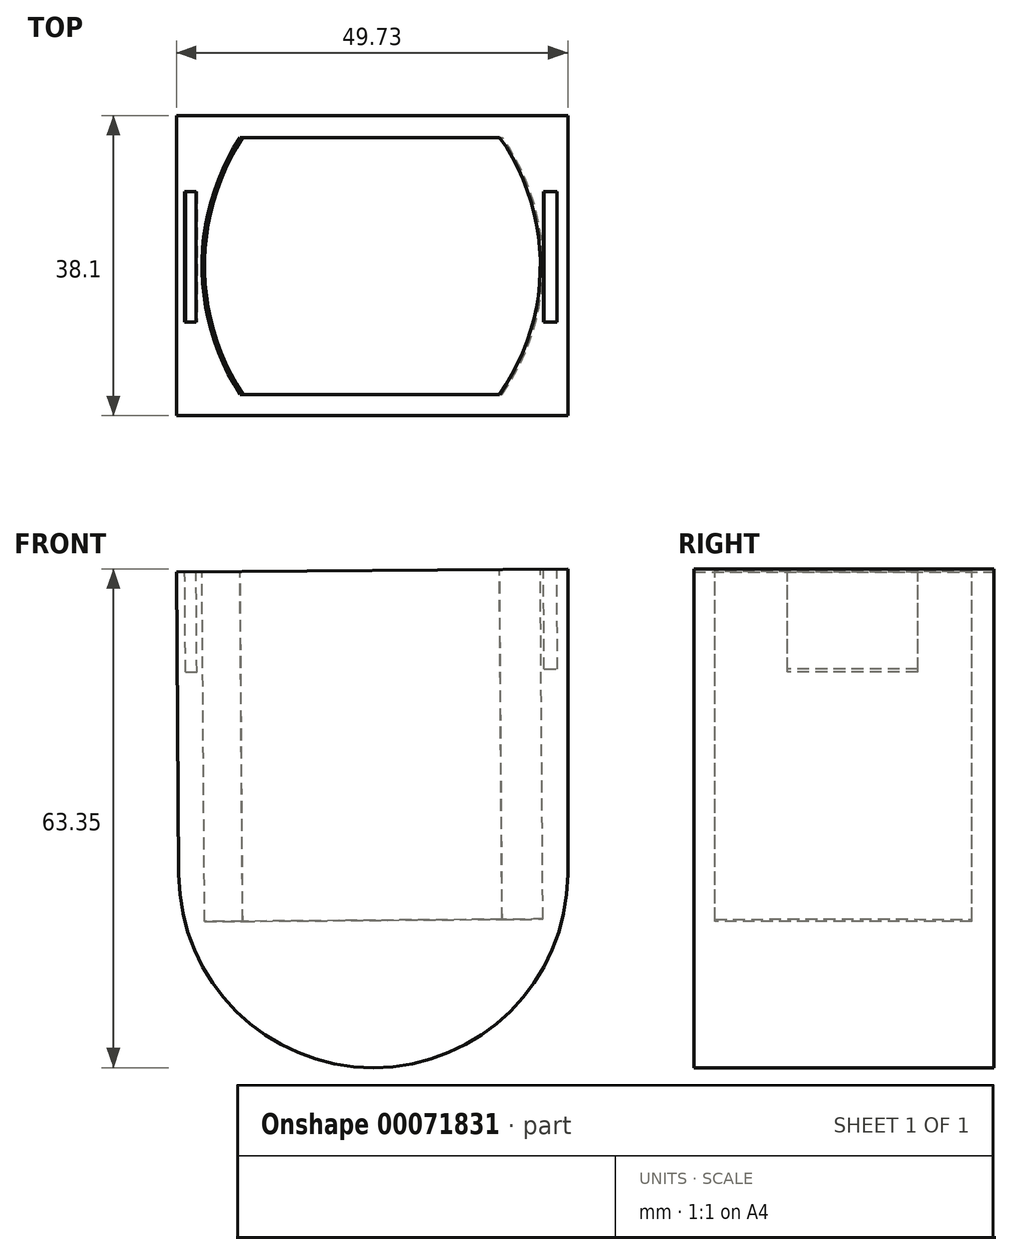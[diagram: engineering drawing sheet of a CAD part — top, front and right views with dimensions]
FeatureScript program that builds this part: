
annotation { "Feature Type Name" : "Feature", "Feature Type Description" : "" }
export const myFeature = defineFeature(function(context is Context, id is Id, definition is map)
    precondition{}
    {
        {
            var Q0;
            Q0=qCreatedBy(makeId("Front.planeOp"),FACE);
            var sketch = newSketch(context, id + "F0", { "sketchPlane" : qUnion([Q0])});
            skArc(sketch, "E0", {"start": v(-24.82, 0) * mm, "mid": v(-0.1, -24.53) * mm, "end": v(24.62, 0) * mm});
            skLineSegment(sketch, "E1", {"start": v(-24.82, 0) * mm, "end": v(-25.1, 38.45) * mm});
            skLineSegment(sketch, "E2", {"start": v(-25.1, 38.45) * mm, "end": v(24.62, 38.82) * mm});
            skLineSegment(sketch, "E3", {"start": v(24.62, 38.82) * mm, "end": v(24.62, 0) * mm});
            skSolve(sketch);
        }
        {
            var Q0;
            Q0=makeQuery(id+"F0.imprint","IMPRINT",FACE,{"disambiguationData":[TD([[makeQuery(id+"F0.imprint","IMPRINT",EDGE,{"derivedFrom":sQuery(id+"F0.wireOp",EDGE,"E0")}),1.0]])]});
            extrude(context, id + "F1", {"entities" : qUnion([Q0]), "depth" : 38.1 * mm});
        }
        {
            var Q0;
            Q0=makeQuery(id+"F1.opExtrude","SWEPT_FACE",FACE,{"disambiguationData":[OSD([sQuery(id+"F0.wireOp",EDGE,"E2")])]});
            var sketch = newSketch(context, id + "F2", { "sketchPlane" : qUnion([Q0])});
            skLineSegment(sketch, "E4", {"start": v(16.21, -35.41) * mm, "end": v(-16.71, -35.41) * mm});
            skLineSegment(sketch, "E5", {"start": v(-16.75, -2.78) * mm, "end": v(16.25, -2.78) * mm});
            skArc(sketch, "E6", {"start": v(-16.75, -2.78) * mm, "mid": v(-21.57, -19.1) * mm, "end": v(-16.71, -35.41) * mm});
            skArc(sketch, "E7", {"start": v(16.21, -35.41) * mm, "mid": v(21.4, -19.1) * mm, "end": v(16.25, -2.78) * mm});
            skSolve(sketch);
        }
        {
            var Q0;
            Q0=makeQuery(id+"F2.imprint","IMPRINT",FACE,{"disambiguationData":[TD([[makeQuery(id+"F2.imprint","IMPRINT",EDGE,{"derivedFrom":sQuery(id+"F2.wireOp",EDGE,"E4")}),-1.0]])]});
            extrude(context, id + "F3", {"entities" : qUnion([Q0]), "operationType" : NewBodyOperationType.REMOVE, "oppositeDirection" : true, "depth" : 44.45 * mm});
        }
        {
            var Q0;
            Q0=makeQuery(id+"F1.opExtrude","SWEPT_FACE",FACE,{"disambiguationData":[OSD([sQuery(id+"F0.wireOp",EDGE,"E2")])]});
            var sketch = newSketch(context, id + "F4", { "sketchPlane" : qUnion([Q0])});
            skLineSegment(sketch, "E8.bottom", {"start": v(-23.76, -9.66) * mm, "end": v(-22.31, -9.66) * mm});
            skLineSegment(sketch, "E8.top", {"start": v(-23.76, -26.2) * mm, "end": v(-22.31, -26.2) * mm});
            skLineSegment(sketch, "E8.left", {"start": v(-23.76, -9.66) * mm, "end": v(-23.76, -26.2) * mm});
            skLineSegment(sketch, "E8.right", {"start": v(-22.31, -9.66) * mm, "end": v(-22.31, -26.2) * mm});
            skLineSegment(sketch, "E9.bottom", {"start": v(21.8, -9.66) * mm, "end": v(23.5, -9.66) * mm});
            skLineSegment(sketch, "E9.top", {"start": v(21.8, -26.2) * mm, "end": v(23.5, -26.2) * mm});
            skLineSegment(sketch, "E9.left", {"start": v(21.8, -9.66) * mm, "end": v(21.8, -26.2) * mm});
            skLineSegment(sketch, "E9.right", {"start": v(23.5, -9.66) * mm, "end": v(23.5, -26.2) * mm});
            skSolve(sketch);
        }
        {
            var Q0;
            Q0=makeQuery(id+"F4.imprint","IMPRINT",FACE,{"disambiguationData":[TD([[makeQuery(id+"F4.imprint","IMPRINT",EDGE,{"derivedFrom":sQuery(id+"F4.wireOp",EDGE,"E8.bottom")}),-1.0]])]});
            extrude(context, id + "F5", {"entities" : qUnion([Q0]), "operationType" : NewBodyOperationType.REMOVE, "oppositeDirection" : true, "depth" : 12.7 * mm});
        }
        {
            var Q0;
            Q0 = qSketchRegion(id + "F4", true);
            extrude(context, id + "F6", {"entities" : qUnion([Q0]), "operationType" : NewBodyOperationType.REMOVE, "oppositeDirection" : true, "depth" : 12.7 * mm});
        }
    });
